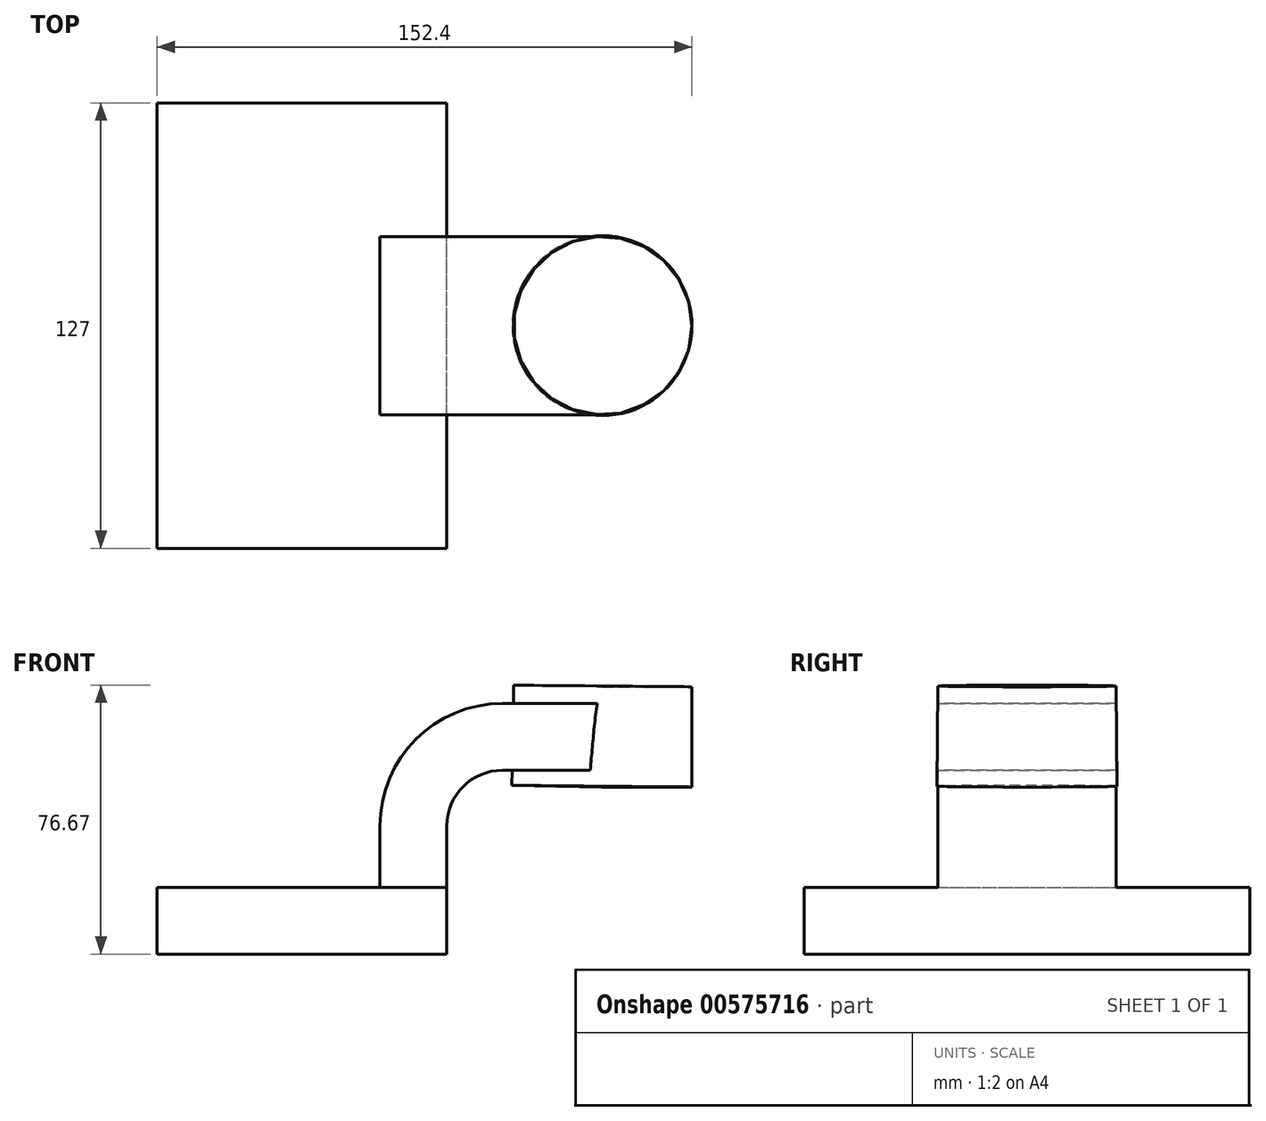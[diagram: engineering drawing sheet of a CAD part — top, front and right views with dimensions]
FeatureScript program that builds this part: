
annotation { "Feature Type Name" : "Feature", "Feature Type Description" : "" }
export const myFeature = defineFeature(function(context is Context, id is Id, definition is map)
    precondition{}
    {
        {
            var Q0;
            Q0=qCreatedBy(makeId("Front.planeOp"),FACE);
            var sketch = newSketch(context, id + "F0", { "sketchPlane" : qUnion([Q0])});
            skLineSegment(sketch, "E0.bottom", {"start": v(-41.28, -9.53) * mm, "end": v(41.28, -9.53) * mm});
            skLineSegment(sketch, "E0.top", {"start": v(-41.28, 9.53) * mm, "end": v(41.28, 9.53) * mm});
            skLineSegment(sketch, "E0.left", {"start": v(-41.27, -9.53) * mm, "end": v(-41.27, 9.53) * mm});
            skLineSegment(sketch, "E0.right", {"start": v(41.28, -9.53) * mm, "end": v(41.28, 9.52) * mm});
            skPoint(sketch, "E0.middle", {"position": v(0, 0) * mm});
            skLineSegment(sketch, "E1.bottom", {"start": v(60.32, 38.1) * mm, "end": v(111.12, 38.1) * mm});
            skLineSegment(sketch, "E1.top", {"start": v(60.32, 66.67) * mm, "end": v(111.12, 66.67) * mm});
            skLineSegment(sketch, "E1.left", {"start": v(60.32, 38.1) * mm, "end": v(60.32, 66.67) * mm});
            skLineSegment(sketch, "E1.right", {"start": v(111.12, 38.1) * mm, "end": v(111.12, 66.67) * mm});
            skPoint(sketch, "E1.middle", {"position": v(85.72, 52.39) * mm});
            skLineSegment(sketch, "E2", {"start": v(41.28, 9.53) * mm, "end": v(41.28, 27) * mm});
            skArc(sketch, "E3", {"start": v(41.27, 27) * mm, "mid": v(45.92, 38.23) * mm, "end": v(57.15, 42.88) * mm});
            skLineSegment(sketch, "E4", {"start": v(57.15, 42.88) * mm, "end": v(85.46, 42.88) * mm});
            skLineSegment(sketch, "E5.0", {"start": v(57.15, 61.93) * mm, "end": v(85.46, 61.93) * mm});
            skArc(sketch, "E5.1", {"start": v(22.23, 27) * mm, "mid": v(32.45, 51.7) * mm, "end": v(57.15, 61.93) * mm});
            skLineSegment(sketch, "E5.2", {"start": v(22.22, 9.53) * mm, "end": v(22.22, 27) * mm});
            skLineSegment(sketch, "E6", {"start": v(85.46, 42.88) * mm, "end": v(85.46, 61.93) * mm});
            skFitSpline(sketch, "E7", {"points": [v(-41.28, 9.52) * mm, v(57.15, 61.93) * mm], "startDerivative": vector(0, 97.83) * mm, "endDerivative": vector(115.47, 0) * mm});
            skLineSegment(sketch, "E8", {"start": v(85.72, 66.67) * mm, "end": v(85.46, 38.1) * mm});
            skSolve(sketch);
        }
        {
            var Q0;
            Q0=makeQuery(id+"F0.imprint","IMPRINT",FACE,{"disambiguationData":[TD([[makeQuery(id+"F0.imprint","IMPRINT",EDGE,{"derivedFrom":sQuery(id+"F0.wireOp",EDGE,"E0.bottom")}),1.0]])]});
            extrude(context, id + "F1", {"entities" : qUnion([Q0]), "endBound" : BoundingType.SYMMETRIC, "depth" : 127 * mm, "offsetDistance" : 25.4 * mm});
        }
        {
            var Q0;
            {var subQ0=sQuery(id+"F0.wireOp",EDGE,"E2");Q0=makeQuery(id+"F0.imprint","IMPRINT",FACE,{"disambiguationData":[TD([[makeQuery(id+"F0.imprint","IMPRINT",EDGE,{"derivedFrom":subQ0}),1.0]])]});}
            var Q1;
            {var subQ5=sQuery(id+"F0.wireOp",EDGE,"E6");Q1=makeQuery(id+"F0.imprint","IMPRINT",FACE,{"disambiguationData":[TD([[makeQuery(id+"F0.imprint","IMPRINT",EDGE,{"derivedFrom":subQ5}),1.0]])]});}
            extrude(context, id + "F2", {"entities" : qUnion([Q0, Q1]), "operationType" : NewBodyOperationType.ADD, "endBound" : BoundingType.SYMMETRIC, "depth" : 50.8 * mm, "offsetDistance" : 25.4 * mm});
        }
        {
            var Q0;
            Q0=makeQuery(id+"F0.imprint","IMPRINT",FACE,{"disambiguationData":[TD([[makeQuery(id+"F0.imprint","IMPRINT",EDGE,{"derivedFrom":sQuery(id+"F0.wireOp",EDGE,"E5.1")}),1.0]])]});
            extrude(context, id + "F3", {"entities" : qUnion([Q0]), "operationType" : NewBodyOperationType.ADD, "endBound" : BoundingType.SYMMETRIC, "depth" : 15.88 * mm, "offsetDistance" : 25.4 * mm});
        }
        {
            var Q0;
            {var subQ0=sQuery(id+"F0.wireOp",EDGE,"E1.right");Q0=makeQuery(id+"F0.imprint","IMPRINT",FACE,{"disambiguationData":[TD([[makeQuery(id+"F0.imprint","IMPRINT",EDGE,{"derivedFrom":subQ0}),1.0]])]});}
            var Q1;
            Q1=sQuery(id+"F0.wireOp",EDGE,"E8");
            revolve(context, id + "F4", {"operationType" : NewBodyOperationType.ADD, "entities" : qUnion([Q0]), "axis" : qUnion([Q1]), "revolveType" : RevolveType.FULL});
        }
    });
